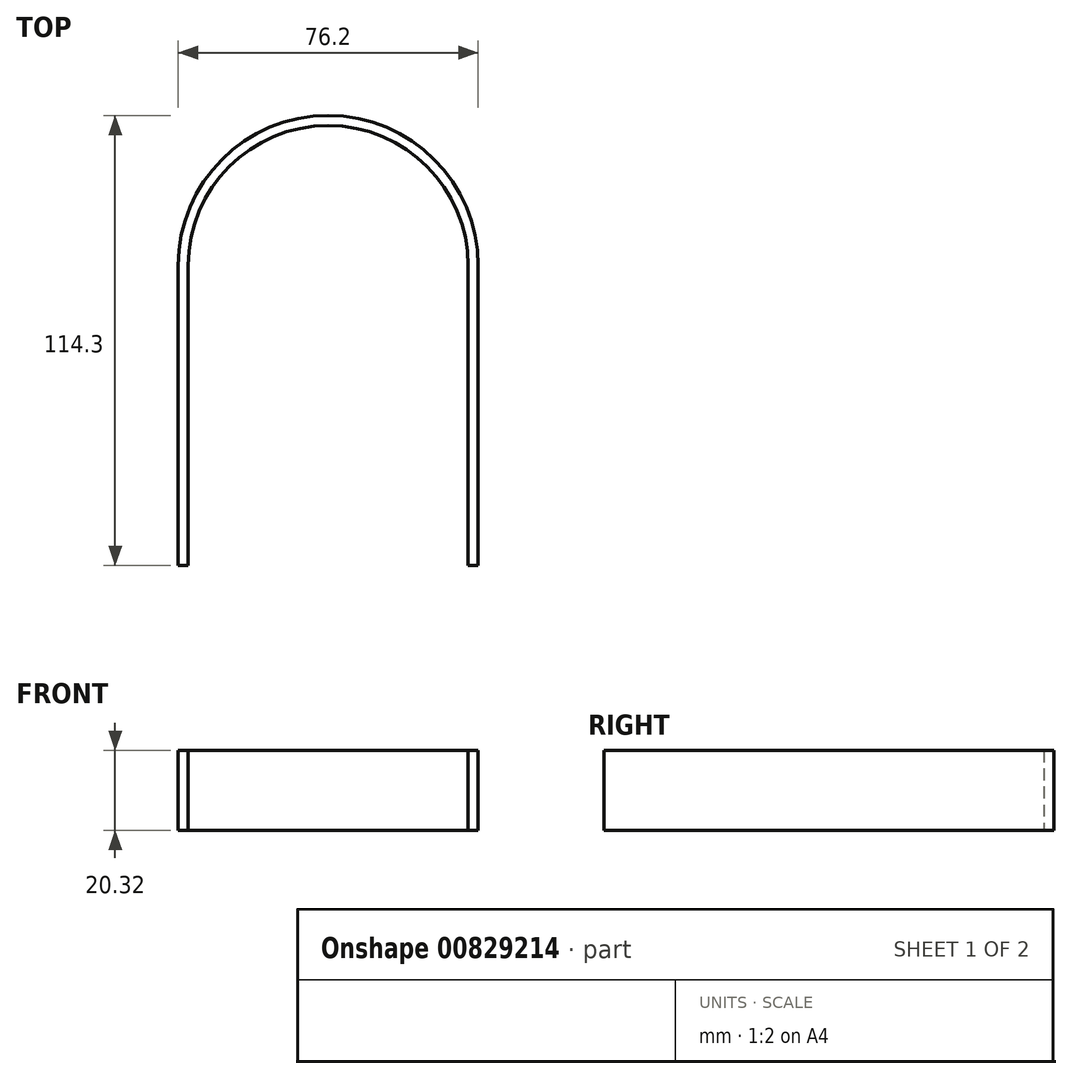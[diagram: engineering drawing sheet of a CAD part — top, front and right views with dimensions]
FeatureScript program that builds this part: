
annotation { "Feature Type Name" : "Feature", "Feature Type Description" : "" }
export const myFeature = defineFeature(function(context is Context, id is Id, definition is map)
    precondition{}
    {
        {
            var Q0;
            Q0=qCreatedBy(makeId("Top.planeOp"),FACE);
            var sketch = newSketch(context, id + "F0", { "sketchPlane" : qUnion([Q0])});
            skLineSegment(sketch, "E0.bottom", {"start": v(38.1, -38.1) * mm, "end": v(-38.1, -38.1) * mm});
            skLineSegment(sketch, "E0.top", {"start": v(38.1, 38.1) * mm, "end": v(-38.1, 38.1) * mm});
            skLineSegment(sketch, "E0.left", {"start": v(38.1, -38.1) * mm, "end": v(38.1, 38.1) * mm});
            skLineSegment(sketch, "E0.right", {"start": v(-38.1, -38.1) * mm, "end": v(-38.1, 38.1) * mm});
            skPoint(sketch, "E0.middle", {"position": v(0, 0) * mm});
            skArc(sketch, "E1", {"start": v(38.1, 38.1) * mm, "mid": v(0, 76.2) * mm, "end": v(-38.1, 38.1) * mm});
            skSolve(sketch);
        }
        {
            var Q0;
            Q0=makeQuery(id+"F0.imprint","IMPRINT",FACE,{"disambiguationData":[TD([[makeQuery(id+"F0.imprint","IMPRINT",EDGE,{"derivedFrom":sQuery(id+"F0.wireOp",EDGE,"E0.bottom")}),-1.0]])]});
            var Q1;
            Q1=makeQuery(id+"F0.imprint","IMPRINT",FACE,{"disambiguationData":[TD([[makeQuery(id+"F0.imprint","IMPRINT",EDGE,{"derivedFrom":sQuery(id+"F0.wireOp",EDGE,"E0.top")}),-1.0]])]});
            extrude(context, id + "F1", {"entities" : qUnion([Q0, Q1]), "depth" : 20.07 * mm, "offsetDistance" : 25.4 * mm});
        }
        {
            var Q0;
            Q0=makeQuery(id+"F1.opExtrude","CAP_FACE",FACE,{"disambiguationData":[OSD([sQuery(id+"F0.wireOp",EDGE,"E0.bottom"),sQuery(id+"F0.wireOp",EDGE,"E0.left"),sQuery(id+"F0.wireOp",EDGE,"E0.right"),sQuery(id+"F0.wireOp",EDGE,"E1")])],"isStart":false});
            extrude(context, id + "F2", {"entities" : qUnion([Q0]), "operationType" : NewBodyOperationType.ADD, "depth" : 0.25 * mm, "offsetDistance" : 25.4 * mm});
        }
        {
            var Q0;
            {var subQ0=sQuery(id+"F0.wireOp",EDGE,"E0.bottom");Q0=makeQuery(id+"F2.boolean.opBoolean","MERGE",FACE,{"derivedFrom":[makeQuery(id+"F1.opExtrude","SWEPT_FACE",FACE,{"disambiguationData":[OSD([subQ0])]}),makeQuery(id+"F2.opExtrude","SWEPT_FACE",FACE,{"disambiguationData":[OSD([subQ0])]})]});}
            var Q1;
            Q1=makeQuery(id+"F2.opExtrude","CAP_FACE",FACE,{"disambiguationData":[OSD([sQuery(id+"F0.wireOp",EDGE,"E0.bottom"),sQuery(id+"F0.wireOp",EDGE,"E0.left"),sQuery(id+"F0.wireOp",EDGE,"E0.right"),sQuery(id+"F0.wireOp",EDGE,"E1")])],"isStart":false});
            var Q2;
            Q2=makeQuery(id+"F1.opExtrude","CAP_FACE",FACE,{"disambiguationData":[OSD([sQuery(id+"F0.wireOp",EDGE,"E0.bottom"),sQuery(id+"F0.wireOp",EDGE,"E0.left"),sQuery(id+"F0.wireOp",EDGE,"E0.right"),sQuery(id+"F0.wireOp",EDGE,"E1")])],"isStart":true});
            shell(context, id + "F3", {"entities" : qUnion([Q0, Q1, Q2]), "thickness" : 2.54 * mm});
        }
    });
